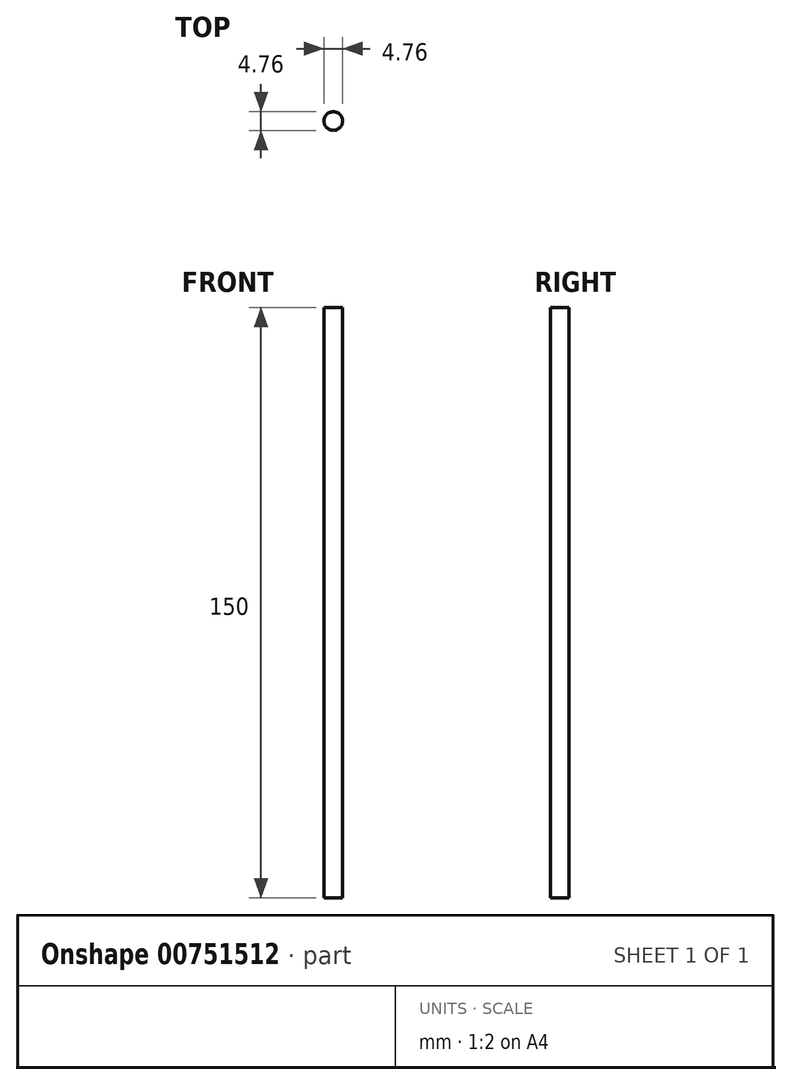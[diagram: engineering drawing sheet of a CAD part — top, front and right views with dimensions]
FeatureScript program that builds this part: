
annotation { "Feature Type Name" : "Feature", "Feature Type Description" : "" }
export const myFeature = defineFeature(function(context is Context, id is Id, definition is map)
    precondition{}
    {
        {
            var Q0;
            Q0=qCreatedBy(makeId("Top.planeOp"),FACE);
            var sketch = newSketch(context, id + "F0", { "sketchPlane" : qUnion([Q0])});
            skCircle(sketch, "E0", {"center": v(0, 0) * mm, "radius": 2.38 * mm});
            skSolve(sketch);
        }
        {
            var Q0;
            Q0=makeQuery(id+"F0.imprint","IMPRINT",FACE,{"disambiguationData":[TD([[makeQuery(id+"F0.imprint","IMPRINT",EDGE,{"derivedFrom":sQuery(id+"F0.wireOp",EDGE,"E0")}),1.0]])]});
            extrude(context, id + "F1", {"entities" : qUnion([Q0]), "depth" : 150 * mm, "offsetDistance" : 25 * mm});
        }
    });
